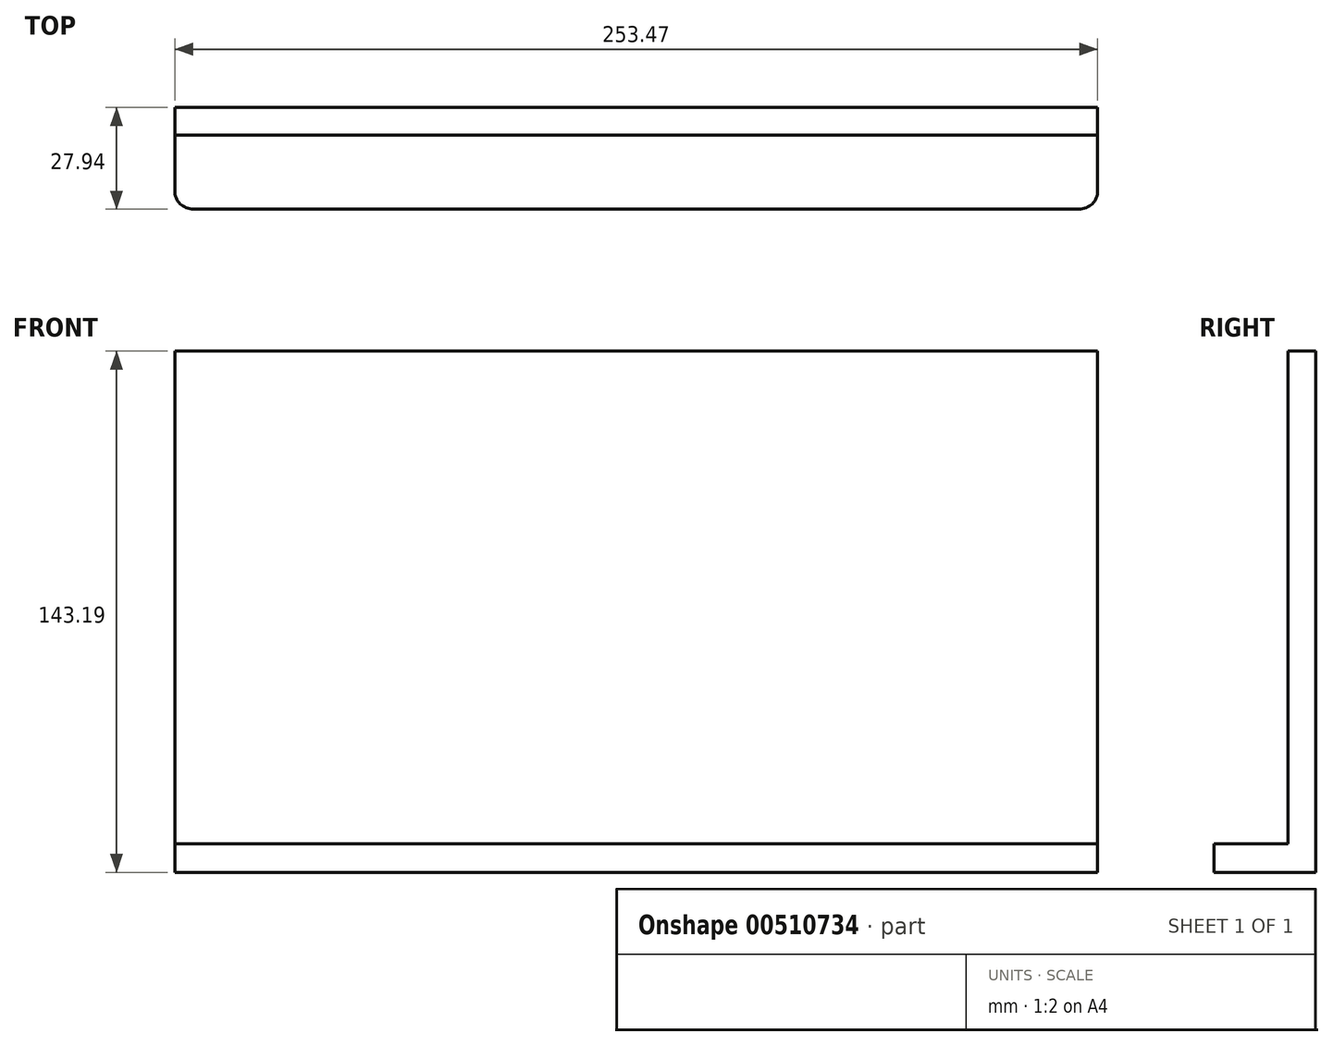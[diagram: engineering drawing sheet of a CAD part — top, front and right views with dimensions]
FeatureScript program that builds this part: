
annotation { "Feature Type Name" : "Feature", "Feature Type Description" : "" }
export const myFeature = defineFeature(function(context is Context, id is Id, definition is map)
    precondition{}
    {
        {
            var Q0;
            Q0=qCreatedBy(makeId("Front.planeOp"),FACE);
            var sketch = newSketch(context, id + "F0", { "sketchPlane" : qUnion([Q0])});
            skLineSegment(sketch, "E0.bottom", {"start": v(-127.78, 77.53) * mm, "end": v(125.69, 77.53) * mm});
            skLineSegment(sketch, "E0.top", {"start": v(-127.78, -65.66) * mm, "end": v(125.69, -65.66) * mm});
            skLineSegment(sketch, "E0.left", {"start": v(-127.78, 77.53) * mm, "end": v(-127.78, -65.66) * mm});
            skLineSegment(sketch, "E0.right", {"start": v(125.69, 77.53) * mm, "end": v(125.69, -65.66) * mm});
            skSolve(sketch);
        }
        {
            var Q0;
            Q0=makeQuery(id+"F0.imprint","IMPRINT",FACE,{"disambiguationData":[TD([[makeQuery(id+"F0.imprint","IMPRINT",EDGE,{"derivedFrom":sQuery(id+"F0.wireOp",EDGE,"E0.bottom")}),-1.0]])]});
            extrude(context, id + "F1", {"entities" : qUnion([Q0]), "depth" : 7.62 * mm});
        }
        {
            var Q0;
            Q0=makeQuery(id+"F1.opExtrude","CAP_FACE",FACE,{"disambiguationData":[OSD([sQuery(id+"F0.wireOp",EDGE,"E0.bottom"),sQuery(id+"F0.wireOp",EDGE,"E0.top"),sQuery(id+"F0.wireOp",EDGE,"E0.left"),sQuery(id+"F0.wireOp",EDGE,"E0.right")])],"isStart":false});
            var sketch = newSketch(context, id + "F2", { "sketchPlane" : qUnion([Q0])});
            skLineSegment(sketch, "E1", {"start": v(-127.78, -65.66) * mm, "end": v(125.69, -65.66) * mm});
            skLineSegment(sketch, "E2", {"start": v(-127.78, -65.66) * mm, "end": v(-127.78, -57.8) * mm});
            skLineSegment(sketch, "E3", {"start": v(-127.78, -57.8) * mm, "end": v(125.69, -57.8) * mm});
            skLineSegment(sketch, "E4", {"start": v(125.69, -57.8) * mm, "end": v(125.69, -65.66) * mm});
            skSolve(sketch);
        }
        {
            var Q0;
            Q0=makeQuery(id+"F2.imprint","IMPRINT",FACE,{"disambiguationData":[TD([[makeQuery(id+"F2.imprint","IMPRINT",EDGE,{"derivedFrom":sQuery(id+"F2.wireOp",EDGE,"E1")}),1.0]])]});
            extrude(context, id + "F3", {"entities" : qUnion([Q0]), "operationType" : NewBodyOperationType.ADD, "depth" : 20.32 * mm});
        }
        {
            var Q0;
            Q0=makeQuery(id+"F3.opExtrude","CAP_EDGE",EDGE,{"disambiguationData":[OSD([sQuery(id+"F2.wireOp",EDGE,"E2")])],"isStart":false});
            fillet(context, id + "F4", {"entities" : qUnion([Q0]), "radius" : 5.08 * mm, "tangentPropagation" : true, "allowEdgeOverflow" : false});
        }
        {
            var Q0;
            Q0=makeQuery(id+"F3.opExtrude","CAP_EDGE",EDGE,{"disambiguationData":[OSD([sQuery(id+"F2.wireOp",EDGE,"E4")])],"isStart":false});
            fillet(context, id + "F5", {"entities" : qUnion([Q0]), "radius" : 5.08 * mm, "tangentPropagation" : true, "allowEdgeOverflow" : false});
        }
    });
